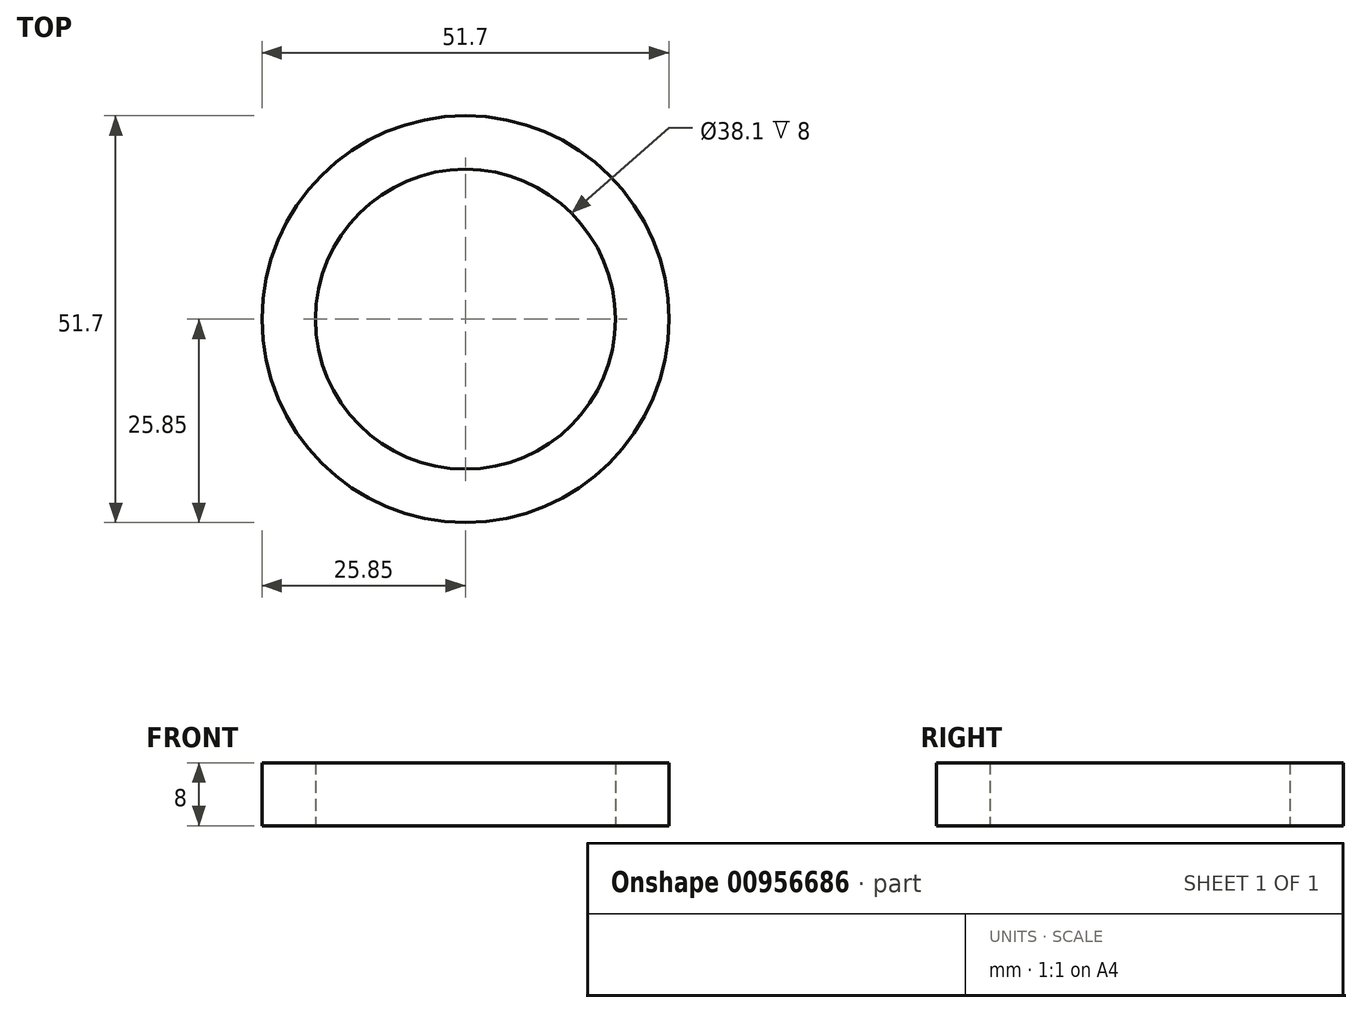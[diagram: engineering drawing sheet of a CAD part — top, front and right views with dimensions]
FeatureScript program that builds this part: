
annotation { "Feature Type Name" : "Feature", "Feature Type Description" : "" }
export const myFeature = defineFeature(function(context is Context, id is Id, definition is map)
    precondition{}
    {
        {
            var Q0;
            Q0=qCreatedBy(makeId("Top.planeOp"),FACE);
            var sketch = newSketch(context, id + "F0", { "sketchPlane" : qUnion([Q0])});
            skCircle(sketch, "E0", {"center": v(0, 0) * mm, "radius": 19.05 * mm});
            skCircle(sketch, "E1", {"center": v(0, 0) * mm, "radius": 25.85 * mm});
            skSolve(sketch);
        }
        {
            var Q0;
            Q0 = qSketchRegion(id + "F0", true);
            var Q1;
            Q1=makeQuery(id+"F0.imprint","IMPRINT",FACE,{"disambiguationData":[TD([[makeQuery(id+"F0.imprint","IMPRINT",EDGE,{"derivedFrom":sQuery(id+"F0.wireOp",EDGE,"E0")}),-1.0]])]});
            extrude(context, id + "F1", {"entities" : qUnion([Q0, Q1]), "depth" : 8 * mm, "offsetDistance" : 25.4 * mm});
        }
    });
